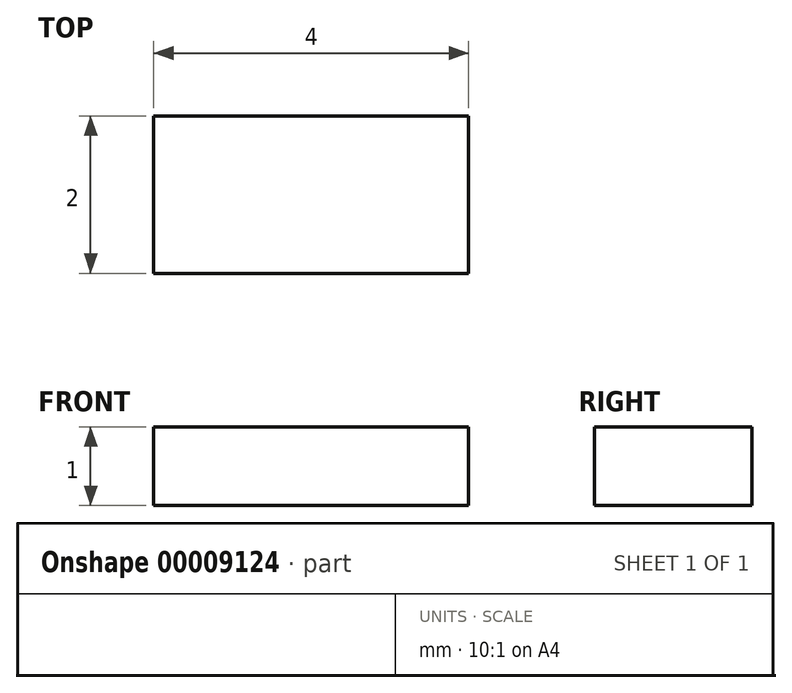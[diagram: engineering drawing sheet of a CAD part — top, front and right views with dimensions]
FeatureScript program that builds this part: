
annotation { "Feature Type Name" : "Feature", "Feature Type Description" : "" }
export const myFeature = defineFeature(function(context is Context, id is Id, definition is map)
    precondition{}
    {
        {
            var Q0;
            Q0=qCreatedBy(makeId("Top.planeOp"),FACE);
            var sketch = newSketch(context, id + "F0", { "sketchPlane" : qUnion([Q0])});
            skLineSegment(sketch, "E0.bottom", {"start": v(-1.81, 2.34) * mm, "end": v(2.19, 2.34) * mm});
            skLineSegment(sketch, "E0.top", {"start": v(-1.81, 0.34) * mm, "end": v(2.19, 0.34) * mm});
            skLineSegment(sketch, "E0.left", {"start": v(-1.81, 2.34) * mm, "end": v(-1.81, 0.34) * mm});
            skLineSegment(sketch, "E0.right", {"start": v(2.19, 2.34) * mm, "end": v(2.19, 0.34) * mm});
            skSolve(sketch);
        }
        {
            var Q0;
            Q0=makeQuery(id+"F0.imprint","IMPRINT",FACE,{"disambiguationData":[TD([[makeQuery(id+"F0.imprint","IMPRINT",EDGE,{"derivedFrom":sQuery(id+"F0.wireOp",EDGE,"E0.bottom")}),-1.0]])]});
            extrude(context, id + "F1", {"entities" : qUnion([Q0]), "depth" : 1 * mm});
        }
    });
